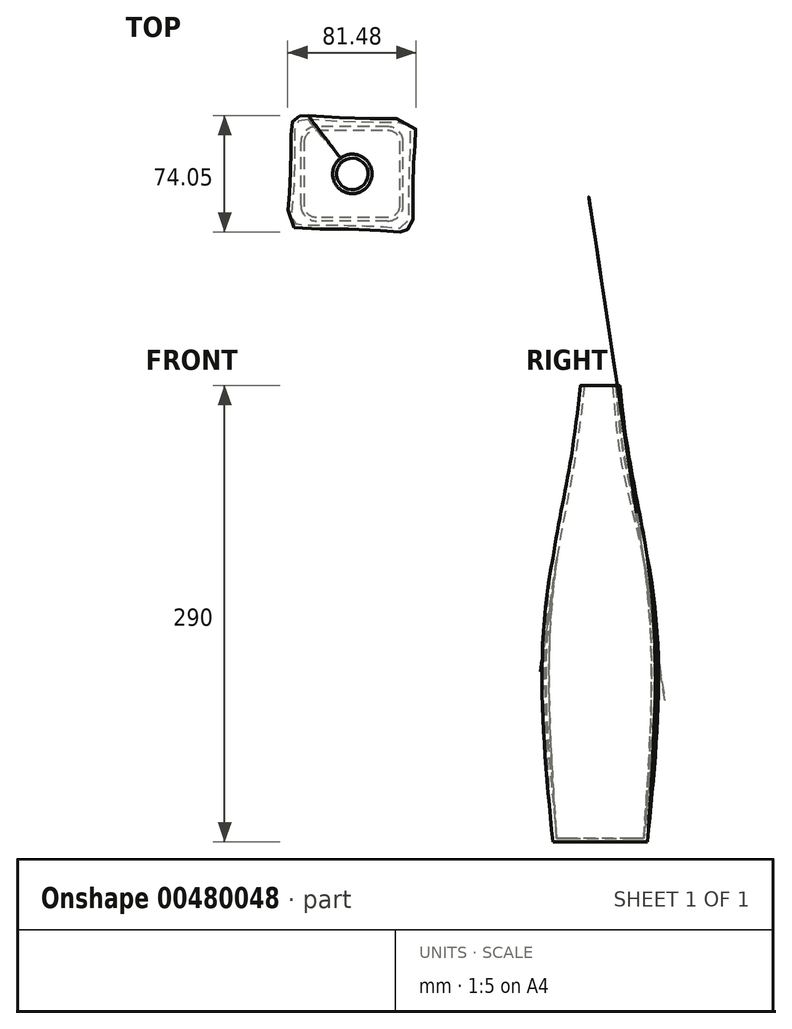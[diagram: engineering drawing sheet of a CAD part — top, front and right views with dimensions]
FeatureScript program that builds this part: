
annotation { "Feature Type Name" : "Feature", "Feature Type Description" : "" }
export const myFeature = defineFeature(function(context is Context, id is Id, definition is map)
    precondition{}
    {
        {
            var Q0;
            Q0=qCreatedBy(makeId("Top.planeOp"),FACE);
            var sketch = newSketch(context, id + "F0", { "sketchPlane" : qUnion([Q0])});
            skLineSegment(sketch, "E0.bottom", {"start": v(25, -30) * mm, "end": v(-20, -30) * mm});
            skLineSegment(sketch, "E0.top", {"start": v(25, 30) * mm, "end": v(-20, 30) * mm});
            skLineSegment(sketch, "E0.left", {"start": v(35, -20) * mm, "end": v(35, 20) * mm});
            skLineSegment(sketch, "E0.right", {"start": v(-30, -20) * mm, "end": v(-30, 20) * mm});
            skPoint(sketch, "E1.visualSharp", {"position": v(-30, -30) * mm});
            skArc(sketch, "E1.filletArc", {"start": v(-30, -20) * mm, "mid": v(-27.07, -27.07) * mm, "end": v(-20, -30) * mm});
            skPoint(sketch, "E2.visualSharp", {"position": v(35, -30) * mm});
            skArc(sketch, "E2.filletArc", {"start": v(25, -30) * mm, "mid": v(32.07, -27.07) * mm, "end": v(35, -20) * mm});
            skPoint(sketch, "E3.visualSharp", {"position": v(35, 30) * mm});
            skArc(sketch, "E3.filletArc", {"start": v(35, 20) * mm, "mid": v(32.07, 27.07) * mm, "end": v(25, 30) * mm});
            skPoint(sketch, "E4.visualSharp", {"position": v(-30, 30) * mm});
            skArc(sketch, "E4.filletArc", {"start": v(-20, 30) * mm, "mid": v(-27.07, 27.07) * mm, "end": v(-30, 20) * mm});
            skSolve(sketch);
        }
        {
            var Q0;
            Q0=qCreatedBy(makeId("Top.planeOp"),FACE);
            cPlane(context, id + "F1", {"entities" : qUnion([Q0]), "cplaneType" : CPlaneType.OFFSET, "offset" : 180 * mm, "width" : 150 * mm, "height" : 150 * mm});
        }
        {
            var Q0;
            Q0=qCreatedBy(id+"F1.planeOp",FACE);
            var sketch = newSketch(context, id + "F2", { "sketchPlane" : qUnion([Q0])});
            skLineSegment(sketch, "E5.bottom", {"start": v(-20.04, 30.05) * mm, "end": v(25, 30.05) * mm});
            skLineSegment(sketch, "E5.top", {"start": v(-20.04, -30) * mm, "end": v(25, -30) * mm});
            skLineSegment(sketch, "E5.left", {"start": v(-30.04, 20.05) * mm, "end": v(-30.04, -20) * mm});
            skLineSegment(sketch, "E5.right", {"start": v(35, 20.05) * mm, "end": v(35, -20) * mm});
            skPoint(sketch, "E6.visualSharp", {"position": v(-30.04, 30.05) * mm});
            skArc(sketch, "E6.filletArc", {"start": v(-20.04, 30.05) * mm, "mid": v(-27.1, 27.12) * mm, "end": v(-30.04, 20.05) * mm});
            skPoint(sketch, "E7.visualSharp", {"position": v(35, 30.05) * mm});
            skArc(sketch, "E7.filletArc", {"start": v(35, 20.05) * mm, "mid": v(32.06, 27.12) * mm, "end": v(25, 30.05) * mm});
            skPoint(sketch, "E8.visualSharp", {"position": v(35, -30) * mm});
            skArc(sketch, "E8.filletArc", {"start": v(25, -30) * mm, "mid": v(32.06, -27.06) * mm, "end": v(35, -20) * mm});
            skPoint(sketch, "E9.visualSharp", {"position": v(-30.04, -30) * mm});
            skArc(sketch, "E9.filletArc", {"start": v(-30.04, -20) * mm, "mid": v(-27.1, -27.06) * mm, "end": v(-20.04, -30) * mm});
            skSolve(sketch);
        }
        {
            var Q0;
            Q0=qCreatedBy(id+"F1.planeOp",FACE);
            cPlane(context, id + "F3", {"entities" : qUnion([Q0]), "cplaneType" : CPlaneType.OFFSET, "offset" : 70 * mm, "width" : 150 * mm, "height" : 150 * mm});
        }
        {
            var Q0;
            Q0=qCreatedBy(id+"F3.planeOp",FACE);
            var sketch = newSketch(context, id + "F4", { "sketchPlane" : qUnion([Q0])});
            skCircle(sketch, "E10", {"center": v(2.69, -0.05) * mm, "radius": 17.5 * mm});
            skSolve(sketch);
        }
        {
            var Q0;
            Q0=qCreatedBy(id+"F3.planeOp",FACE);
            cPlane(context, id + "F5", {"entities" : qUnion([Q0]), "cplaneType" : CPlaneType.OFFSET, "offset" : 40 * mm, "width" : 150 * mm, "height" : 150 * mm});
        }
        {
            var Q0;
            Q0=qCreatedBy(id+"F5.planeOp",FACE);
            var sketch = newSketch(context, id + "F6", { "sketchPlane" : qUnion([Q0])});
            skCircle(sketch, "E11", {"center": v(2.69, -0.05) * mm, "radius": 12.5 * mm});
            skSolve(sketch);
        }
        {
            var Q0;
            Q0=makeQuery(id+"F6.imprint","IMPRINT",FACE,{"disambiguationData":[TD([[makeQuery(id+"F6.imprint","IMPRINT",EDGE,{"derivedFrom":sQuery(id+"F6.wireOp",EDGE,"E11")}),1.0]])]});
            var Q1;
            Q1=makeQuery(id+"F4.imprint","IMPRINT",FACE,{"disambiguationData":[TD([[makeQuery(id+"F4.imprint","IMPRINT",EDGE,{"derivedFrom":sQuery(id+"F4.wireOp",EDGE,"E10")}),1.0]])]});
            var Q2;
            Q2=makeQuery(id+"F2.imprint","IMPRINT",FACE,{"disambiguationData":[TD([[makeQuery(id+"F2.imprint","IMPRINT",EDGE,{"derivedFrom":sQuery(id+"F2.wireOp",EDGE,"E5.bottom")}),-1.0]])]});
            var Q3;
            Q3=makeQuery(id+"F0.imprint","IMPRINT",FACE,{"disambiguationData":[TD([[makeQuery(id+"F0.imprint","IMPRINT",EDGE,{"derivedFrom":sQuery(id+"F0.wireOp",EDGE,"E0.bottom")}),-1.0]])]});
            loft(context, id + "F7", {"sheetProfilesArray" : [{ "sheetProfileEntities" : qUnion([Q0]) }, { "sheetProfileEntities" : qUnion([Q1]) }, { "sheetProfileEntities" : qUnion([Q2]) }, { "sheetProfileEntities" : qUnion([Q3]) }]});
        }
        {
            var Q0;
            Q0=makeQuery(id+"F7.opLoft","CAP_FACE",FACE,{"disambiguationData":[OSD([makeQuery(id+"F6.imprint","IMPRINT",FACE,{"disambiguationData":[TD([[makeQuery(id+"F6.imprint","IMPRINT",EDGE,{"derivedFrom":sQuery(id+"F6.wireOp",EDGE,"E11")}),1.0]])]})])],"isStart":true});
            shell(context, id + "F8", {"entities" : qUnion([Q0]), "thickness" : 2.5 * mm});
        }
    });
